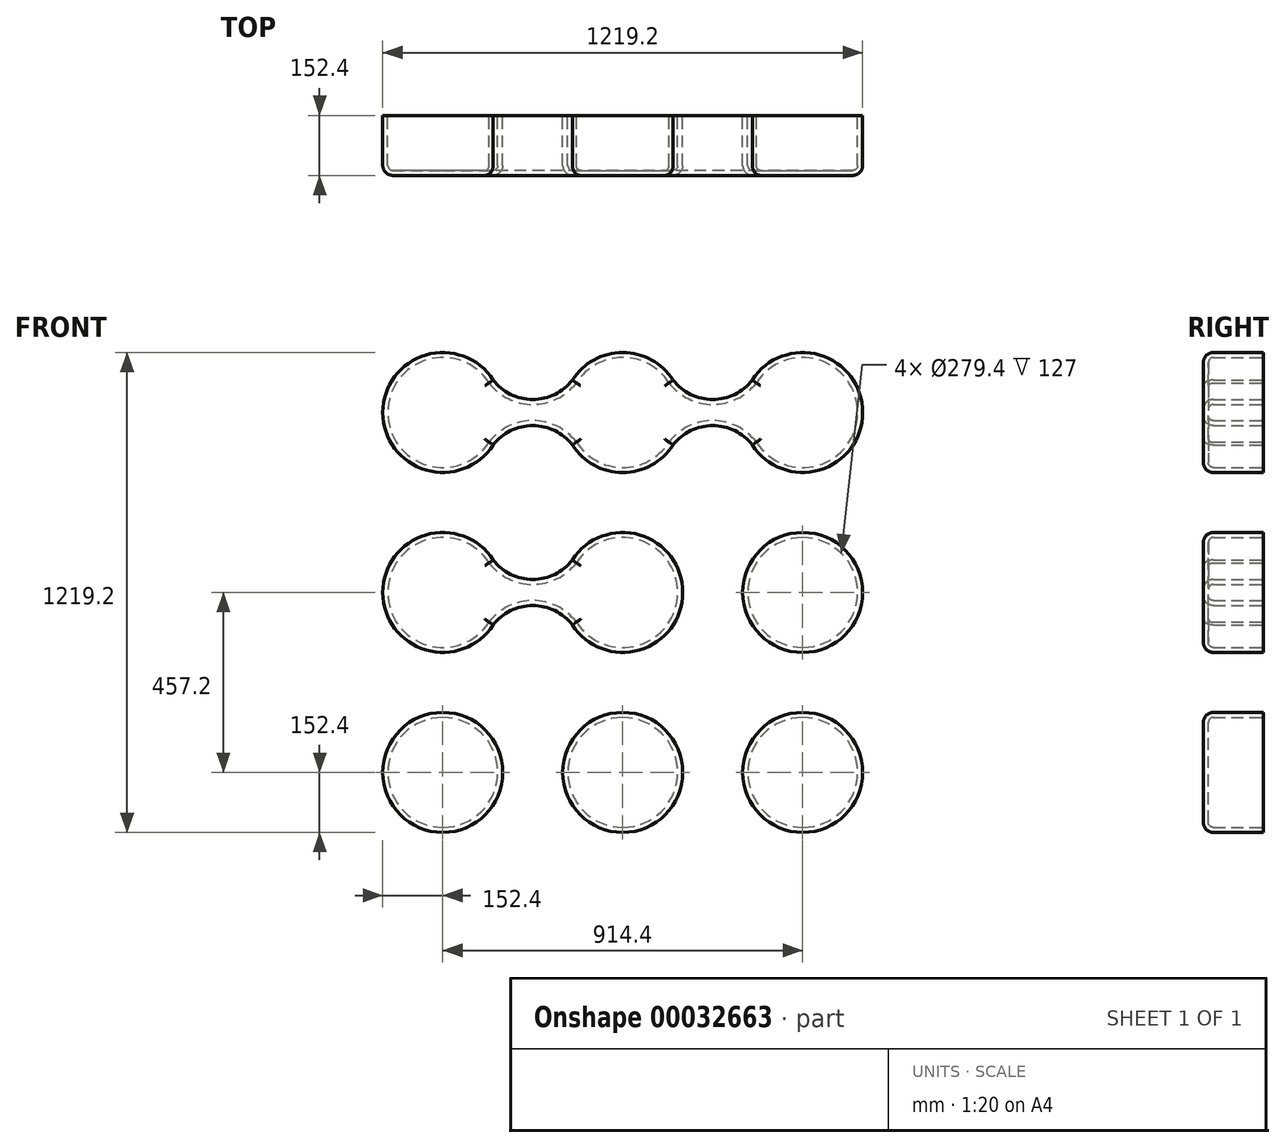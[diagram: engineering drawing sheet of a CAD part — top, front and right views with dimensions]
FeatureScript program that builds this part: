
annotation { "Feature Type Name" : "Feature", "Feature Type Description" : "" }
export const myFeature = defineFeature(function(context is Context, id is Id, definition is map)
    precondition{}
    {
        {
            var Q0;
            Q0=qCreatedBy(makeId("Front.planeOp"),FACE);
            var sketch = newSketch(context, id + "F0", { "sketchPlane" : qUnion([Q0])});
            skArc(sketch, "E0", {"start": v(-128.1, -82.55) * mm, "mid": v(152.4, 0) * mm, "end": v(-128.1, 82.55) * mm});
            skLineSegment(sketch, "E1", {"start": v(0, 0) * mm, "end": v(457.2, 0) * mm, "construction": true});
            skLineSegment(sketch, "E2", {"start": v(0, 0) * mm, "end": v(-457.2, 0) * mm, "construction": true});
            skCircle(sketch, "E3", {"center": v(457.2, 0) * mm, "radius": 152.4 * mm});
            skArc(sketch, "E4", {"start": v(-329.1, 82.55) * mm, "mid": v(-609.6, 0) * mm, "end": v(-329.1, -82.55) * mm});
            skLineSegment(sketch, "E5", {"start": v(457.2, 0) * mm, "end": v(457.2, -457.2) * mm, "construction": true});
            skCircle(sketch, "E6", {"center": v(457.2, -457.2) * mm, "radius": 152.4 * mm});
            skLineSegment(sketch, "E7", {"start": v(457.2, -457.2) * mm, "end": v(0, -457.2) * mm, "construction": true});
            skLineSegment(sketch, "E8", {"start": v(0, -457.2) * mm, "end": v(-457.2, -457.2) * mm, "construction": true});
            skCircle(sketch, "E9", {"center": v(0, -457.2) * mm, "radius": 152.4 * mm});
            skCircle(sketch, "E10", {"center": v(-457.2, -457.2) * mm, "radius": 152.4 * mm});
            skLineSegment(sketch, "E11", {"start": v(457.2, 0) * mm, "end": v(457.2, 457.2) * mm, "construction": true});
            skLineSegment(sketch, "E12", {"start": v(457.2, 457.2) * mm, "end": v(0, 457.2) * mm, "construction": true});
            skLineSegment(sketch, "E13", {"start": v(0, 457.2) * mm, "end": v(-457.2, 457.2) * mm, "construction": true});
            skArc(sketch, "E14", {"start": v(-329.1, 539.75) * mm, "mid": v(-609.6, 457.2) * mm, "end": v(-329.1, 374.65) * mm});
            skArc(sketch, "E15", {"start": v(-128.1, 374.65) * mm, "mid": v(0, 304.8) * mm, "end": v(128.1, 374.65) * mm});
            skArc(sketch, "E16", {"start": v(329.1, 374.65) * mm, "mid": v(609.6, 457.2) * mm, "end": v(329.1, 539.75) * mm});
            skLineSegment(sketch, "E17.0", {"start": v(-128.1, 82.55) * mm, "end": v(-329.1, 82.55) * mm, "construction": true});
            skArc(sketch, "E18", {"start": v(-329.1, 82.55) * mm, "mid": v(-228.6, 33.2) * mm, "end": v(-128.1, 82.55) * mm});
            skArc(sketch, "E19.MirrorCS", {"start": v(-329.1, -82.55) * mm, "mid": v(-228.6, -33.2) * mm, "end": v(-128.1, -82.55) * mm});
            skLineSegment(sketch, "E20.0", {"start": v(-128.1, 539.75) * mm, "end": v(-329.1, 539.75) * mm, "construction": true});
            skLineSegment(sketch, "E21.0", {"start": v(329.1, 539.75) * mm, "end": v(128.1, 539.75) * mm, "construction": true});
            skArc(sketch, "E22", {"start": v(-329.1, 539.75) * mm, "mid": v(-228.6, 490.4) * mm, "end": v(-128.1, 539.75) * mm});
            skArc(sketch, "E23", {"start": v(128.1, 539.75) * mm, "mid": v(228.6, 490.4) * mm, "end": v(329.1, 539.75) * mm});
            skArc(sketch, "E24.MirrorCS", {"start": v(128.1, 374.65) * mm, "mid": v(228.6, 424) * mm, "end": v(329.1, 374.65) * mm});
            skArc(sketch, "E25.MirrorCS", {"start": v(-329.1, 374.65) * mm, "mid": v(-228.6, 424) * mm, "end": v(-128.1, 374.65) * mm});
            skArc(sketch, "E26.trimOffspring", {"start": v(128.1, 539.75) * mm, "mid": v(0, 609.6) * mm, "end": v(-128.1, 539.75) * mm});
            skSolve(sketch);
        }
        {
            var Q0;
            Q0=makeQuery(id+"F0.imprint","IMPRINT",FACE,{"disambiguationData":[TD([[makeQuery(id+"F0.imprint","IMPRINT",EDGE,{"derivedFrom":sQuery(id+"F0.wireOp",EDGE,"E14")}),1.0]])]});
            var Q1;
            Q1=makeQuery(id+"F0.imprint","IMPRINT",FACE,{"disambiguationData":[TD([[makeQuery(id+"F0.imprint","IMPRINT",EDGE,{"derivedFrom":sQuery(id+"F0.wireOp",EDGE,"E0")}),1.0]])]});
            var Q2;
            Q2=makeQuery(id+"F0.imprint","IMPRINT",FACE,{"disambiguationData":[TD([[makeQuery(id+"F0.imprint","IMPRINT",EDGE,{"derivedFrom":sQuery(id+"F0.wireOp",EDGE,"E3")}),1.0]])]});
            var Q3;
            Q3=makeQuery(id+"F0.imprint","IMPRINT",FACE,{"disambiguationData":[TD([[makeQuery(id+"F0.imprint","IMPRINT",EDGE,{"derivedFrom":sQuery(id+"F0.wireOp",EDGE,"E6")}),1.0]])]});
            var Q4;
            Q4=makeQuery(id+"F0.imprint","IMPRINT",FACE,{"disambiguationData":[TD([[makeQuery(id+"F0.imprint","IMPRINT",EDGE,{"derivedFrom":sQuery(id+"F0.wireOp",EDGE,"E9")}),1.0]])]});
            var Q5;
            Q5=makeQuery(id+"F0.imprint","IMPRINT",FACE,{"disambiguationData":[TD([[makeQuery(id+"F0.imprint","IMPRINT",EDGE,{"derivedFrom":sQuery(id+"F0.wireOp",EDGE,"E10")}),1.0]])]});
            extrude(context, id + "F1", {"entities" : qUnion([Q0, Q1, Q2, Q3, Q4, Q5]), "depth" : 152.4 * mm});
        }
        {
            var Q0;
            Q0=makeQuery(id+"F1.opExtrude","CAP_FACE",FACE,{"disambiguationData":[OSD([sQuery(id+"F0.wireOp",EDGE,"E6")])],"isStart":false});
            var Q1;
            Q1=makeQuery(id+"F1.opExtrude","CAP_FACE",FACE,{"disambiguationData":[OSD([sQuery(id+"F0.wireOp",EDGE,"E9")])],"isStart":false});
            var Q2;
            Q2=makeQuery(id+"F1.opExtrude","CAP_FACE",FACE,{"disambiguationData":[OSD([sQuery(id+"F0.wireOp",EDGE,"E10")])],"isStart":false});
            var Q3;
            Q3=makeQuery(id+"F1.opExtrude","CAP_FACE",FACE,{"disambiguationData":[OSD([sQuery(id+"F0.wireOp",EDGE,"E3")])],"isStart":false});
            var Q4;
            Q4=makeQuery(id+"F1.opExtrude","CAP_FACE",FACE,{"disambiguationData":[OSD([sQuery(id+"F0.wireOp",EDGE,"E0"),sQuery(id+"F0.wireOp",EDGE,"E4"),sQuery(id+"F0.wireOp",EDGE,"E18"),sQuery(id+"F0.wireOp",EDGE,"E19.MirrorCS")])],"isStart":false});
            var Q5;
            Q5=makeQuery(id+"F1.opExtrude","CAP_FACE",FACE,{"disambiguationData":[OSD([sQuery(id+"F0.wireOp",EDGE,"E14"),sQuery(id+"F0.wireOp",EDGE,"E15"),sQuery(id+"F0.wireOp",EDGE,"E16"),sQuery(id+"F0.wireOp",EDGE,"E22"),sQuery(id+"F0.wireOp",EDGE,"E23"),sQuery(id+"F0.wireOp",EDGE,"E24.MirrorCS"),sQuery(id+"F0.wireOp",EDGE,"E25.MirrorCS"),sQuery(id+"F0.wireOp",EDGE,"E26.trimOffspring")])],"isStart":false});
            fillet(context, id + "F2", {"entities" : qUnion([Q0, Q1, Q2, Q3, Q4, Q5]), "radius" : 25.4 * mm, "tangentPropagation" : true, "allowEdgeOverflow" : false});
        }
        {
            var Q0;
            Q0=makeQuery(id+"F1.opExtrude","CAP_FACE",FACE,{"disambiguationData":[OSD([sQuery(id+"F0.wireOp",EDGE,"E6")])],"isStart":true});
            var Q1;
            Q1=makeQuery(id+"F1.opExtrude","CAP_FACE",FACE,{"disambiguationData":[OSD([sQuery(id+"F0.wireOp",EDGE,"E9")])],"isStart":true});
            var Q2;
            Q2=makeQuery(id+"F1.opExtrude","CAP_FACE",FACE,{"disambiguationData":[OSD([sQuery(id+"F0.wireOp",EDGE,"E10")])],"isStart":true});
            var Q3;
            Q3=makeQuery(id+"F1.opExtrude","CAP_FACE",FACE,{"disambiguationData":[OSD([sQuery(id+"F0.wireOp",EDGE,"E3")])],"isStart":true});
            var Q4;
            Q4=makeQuery(id+"F1.opExtrude","CAP_FACE",FACE,{"disambiguationData":[OSD([sQuery(id+"F0.wireOp",EDGE,"E0"),sQuery(id+"F0.wireOp",EDGE,"E4"),sQuery(id+"F0.wireOp",EDGE,"E18"),sQuery(id+"F0.wireOp",EDGE,"E19.MirrorCS")])],"isStart":true});
            var Q5;
            Q5=makeQuery(id+"F1.opExtrude","CAP_FACE",FACE,{"disambiguationData":[OSD([sQuery(id+"F0.wireOp",EDGE,"E14"),sQuery(id+"F0.wireOp",EDGE,"E15"),sQuery(id+"F0.wireOp",EDGE,"E16"),sQuery(id+"F0.wireOp",EDGE,"E22"),sQuery(id+"F0.wireOp",EDGE,"E23"),sQuery(id+"F0.wireOp",EDGE,"E24.MirrorCS"),sQuery(id+"F0.wireOp",EDGE,"E25.MirrorCS"),sQuery(id+"F0.wireOp",EDGE,"E26.trimOffspring")])],"isStart":true});
            shell(context, id + "F3", {"entities" : qUnion([Q0, Q1, Q2, Q3, Q4, Q5]), "thickness" : 12.7 * mm});
        }
    });
